# Revit family: 94751-221
name_source: partatom
category: Modelos genéricos
revit_build: Autodesk Revit 2016 (Build: 20150220_1215(x64)
units: mm (PartAtom-declared; Revit-internal decimal feet)

## family parameters
Compartilhado = Não
Corte com vazios quando carregados = Não
Cota do conector redondo = Utilizar diâmetro
Hospedeiro = Face
Pode hospedar o vergalhão = Não
Ponto de cálculo do ambiente = Não
Tipo de parte = Normal

## types (1)
- Square Slider B 4EI 60
    Código de montagem = Square Slider B 4EI 60 - Ref. 94751221
    Descrição = Square Slider B 4EI 60 - Ref. 94751221
    Elevação-padrão = 1219.2  [stored 4 ft]
    Fabricante = Tramontina
    Frequencia = 60 Hz
    Modelo = Square Slider B 4EI 60 - Ref. 94751221
    Nicho de Instalação = 495 x 565
    Potencia Eletrica Total = 7000 W
    Potencia Eletrica das Areas de Aquecimento - 160 diametro = 1,5 Kw
    Potencia Eletrica das Areas de Aquecimento - 180 diametro = 2 kW
    Tensão = 220 V
    URL = tramontina.com.br

note: [stored X ft] marks values corroborated as IEEE doubles in the binary element streams (Revit-internal decimal feet)
